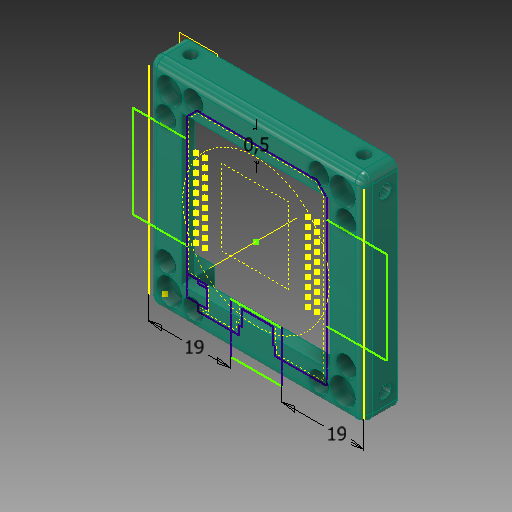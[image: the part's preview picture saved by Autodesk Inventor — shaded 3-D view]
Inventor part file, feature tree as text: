
AUTODESK INVENTOR PART (.ipt)
format: ipt  version: 2019 (Build 230136000, 136)  size: 470,016 bytes
history: native  units: mm
features: reference x13, other x12, sketch x8, hole x6, plane x3, extrude x2, fillet x1, chamfer x1, projected_geometry x1
ambient origin geometry x8: Origin, YZ Plane, XZ Plane, XY Plane, X Axis, Y Axis, Z Axis, Center Point
bodies: Solid1 (feature_tree)
feature tree (47):
  plane  "Work Plane1"
  extrude  "Extrusion1"  Depth=2.0mm
  fillet  "Fillet1"  Radius=49.8mm
  hole  "Hole1"  [1 undecoded]
  other  "Work Axis2"
  hole  "Hole2"  [1 undecoded]
  chamfer  "Chamfer2"  Distance=2.5mm
  hole  "Hole3"  [1 undecoded]
  hole  "Hole4"  [1 undecoded]
  hole  "Hole5"  [1 undecoded]
  extrude  "Extrusion3"  Depth=10.0mm
  sketch  "Sketch13"  dims[d39=2.5mm]
  plane  "Work Plane2"
  plane  "Work Plane3"
  hole  "Hole6"  [1 undecoded]
  sketch  "Sketch1"  dims[d0=7.7mm d1=0.0mm d2=2.0mm]
  reference  "Reference1"
  sketch  "Sketch2"  dims[d10=2.9mm d11=6.0mm d12=6.0mm d13=2.5mm d14=90.0deg d15=6.5mm d16=20.594885mm]
  other  "Work Axis1"
  sketch  "Sketch6"  dims[d20=3.2mm d21=6.0mm d22=6.0mm d23=3.1mm d24=90.0deg d25=12.0mm d26=20.594885mm]
  sketch  "Sketch7"  dims[d27=4.6mm d28=2.0mm d29=45.0deg d34=49.8mm]
  sketch  "Sketch8"  dims[d35=49.8mm d36=5.5mm]
  sketch  "Sketch9"  dims[d37=2.5mm d38=2.5mm]
  reference  "Reference5"
  reference  "Reference6"
  reference  "Reference7"
  reference  "Reference8"
  sketch  "Sketch14"  dims[d40=2.5mm d41=2.5mm d42=2.5mm d43=2.5mm d44=2.5mm d45=2.0mm d46=5.0mm d47=5.0mm d48=5.0mm d49=5.0mm d51=5.0mm d52=0.5mm d53=5.0mm d54=5.0mm d55=2.8mm d56=2.8mm d57=2.8mm d58=2.8mm d59=4.9mm d60=4.9mm d61=4.9mm d62=4.9mm d63=2.8mm d64=2.8mm d65=4.9mm d66=4.9mm d67=4.9mm d68=4.9mm d69=2.8mm d70=6.0mm d71=4.0mm d72=2.0mm d73=90.0deg d74=6.5mm d75=20.594885mm d76=2.8mm d77=6.0mm d78=4.0mm d79=2.0mm d80=90.0deg d81=6.5mm d82=20.594885mm d83=2.8mm d84=6.0mm d85=4.0mm d86=2.0mm d87=90.0deg d88=6.5mm d89=20.594885mm d90=7.7mm d91=135.0deg d92=135.0deg d93=10.0mm d94=0.0mm d100=0.5mm d101=19.0mm d102=19.0mm d105=4.7mm d106=6.0mm d107=4.0mm d108=2.0mm d109=90.0deg d110=8.0mm d111=20.594885mm]
  projected_geometry  "Projected Loop4"
  reference  "Reference9"
  reference  "Reference10"
  reference  "Reference11"
  reference  "Reference12"
  reference  "Reference13"
  reference  "Reference14"
  reference  "Reference15"
  reference  "Reference16"
  other  "<userpath>\Dropbox\UC2\02_CAD\INVENTOR\uc2_v3\Assembly_Cube_empty_1x1_withBase_v3.iam"
  other  "Assembly_Cube_empty_1x1_withBase_v3.iam"
  other  "10_Cube_1x1_v3:1"
  other  "Assembly_Cube_empty_1x1_v2_IM.iam"
  other  "00_ESP32_Mini:1"
  other  "Assembly_Cube_empty_1x1_v2.iam"
  other  "10_Base_v2_puzzle:2"
  other  "10_Cube_1x1_v2_IM:1"
  other  "Assembly_Cube_v2.iam"
  other  "10_Cube_Base:1"
note: 6 required parameter values undecoded (feature->parameter linkage not recoverable at this tier; creation-order binding heuristic only, values carry confidence <= 0.55)
